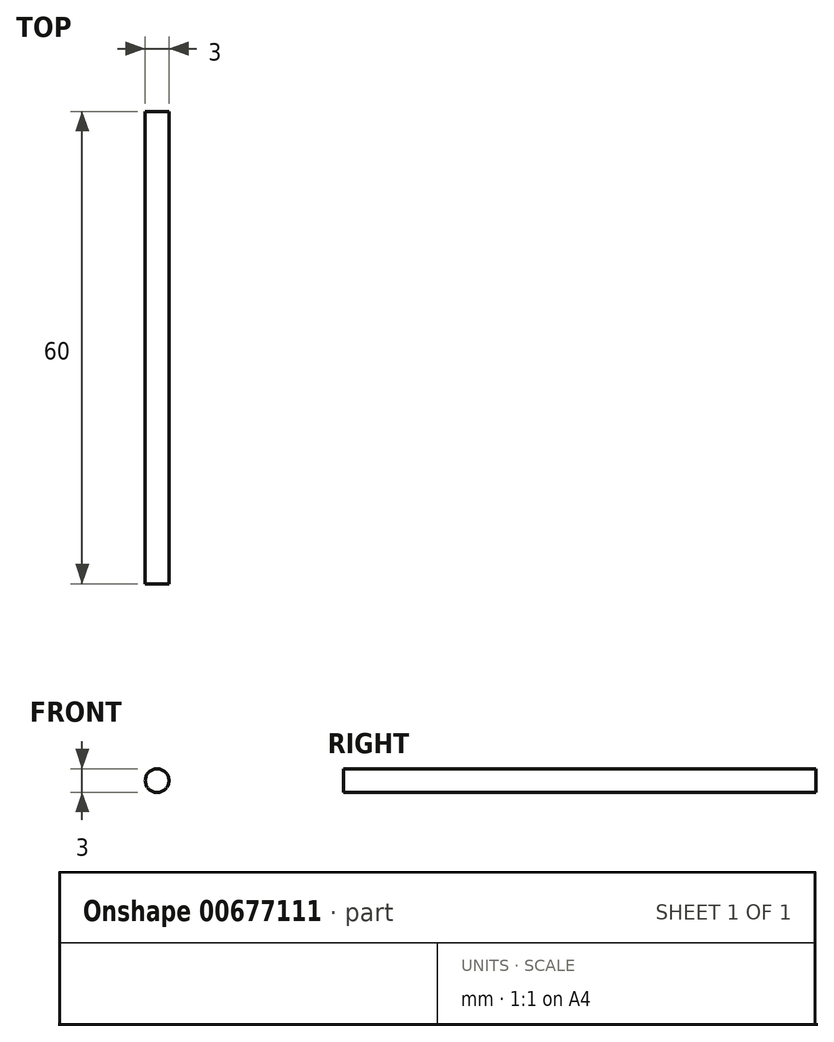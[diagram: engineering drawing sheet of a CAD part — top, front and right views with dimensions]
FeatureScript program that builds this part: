
annotation { "Feature Type Name" : "Feature", "Feature Type Description" : "" }
export const myFeature = defineFeature(function(context is Context, id is Id, definition is map)
    precondition{}
    {
        {
            var Q0;
            Q0=qCreatedBy(makeId("Front.planeOp"),FACE);
            var sketch = newSketch(context, id + "F0", { "sketchPlane" : qUnion([Q0])});
            skCircle(sketch, "E0", {"center": v(0, 0) * mm, "radius": 1.5 * mm});
            skSolve(sketch);
        }
        {
            var Q0;
            Q0 = qSketchRegion(id + "F0", true);
            extrude(context, id + "F1", {"entities" : qUnion([Q0]), "endBound" : BoundingType.SYMMETRIC, "depth" : 60 * mm, "offsetDistance" : 25 * mm});
        }
    });
